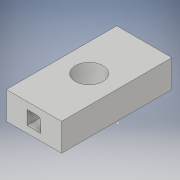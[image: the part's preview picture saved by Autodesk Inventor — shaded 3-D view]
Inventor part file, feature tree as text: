
AUTODESK INVENTOR PART (.ipt)
format: ipt  version: 2018.2 (Build 222227000, 227)  size: 118,272 bytes
history: native  units: in
note: dims shown in document units (in); Inventor stores cm internally (conversion verified against a paired STEP export)
features: sketch x3, extrude x2
ambient origin geometry x8: Origin, YZ Plane, XZ Plane, XY Plane, X Axis, Y Axis, Z Axis, Center Point
bodies: Solid1 (feature_tree)
feature tree (5):
  sketch  "Sketch1"  dims[d0=4.0in d1=2.0in]
  extrude  "Extrusion1"  Depth=2.0in
  extrude  "Extrusion2"  Depth=2.0in
  sketch  "Sketch2"  dims[d2=1.0in d3=2.0in]
  sketch  "Sketch4"  dims[d4=1.0in d5=1.0in d6=0.0in d7=0.5in d8=0.5in d9=0.75in d10=0.251in d11=0.125in d12=1.0in d13=0.0in]
